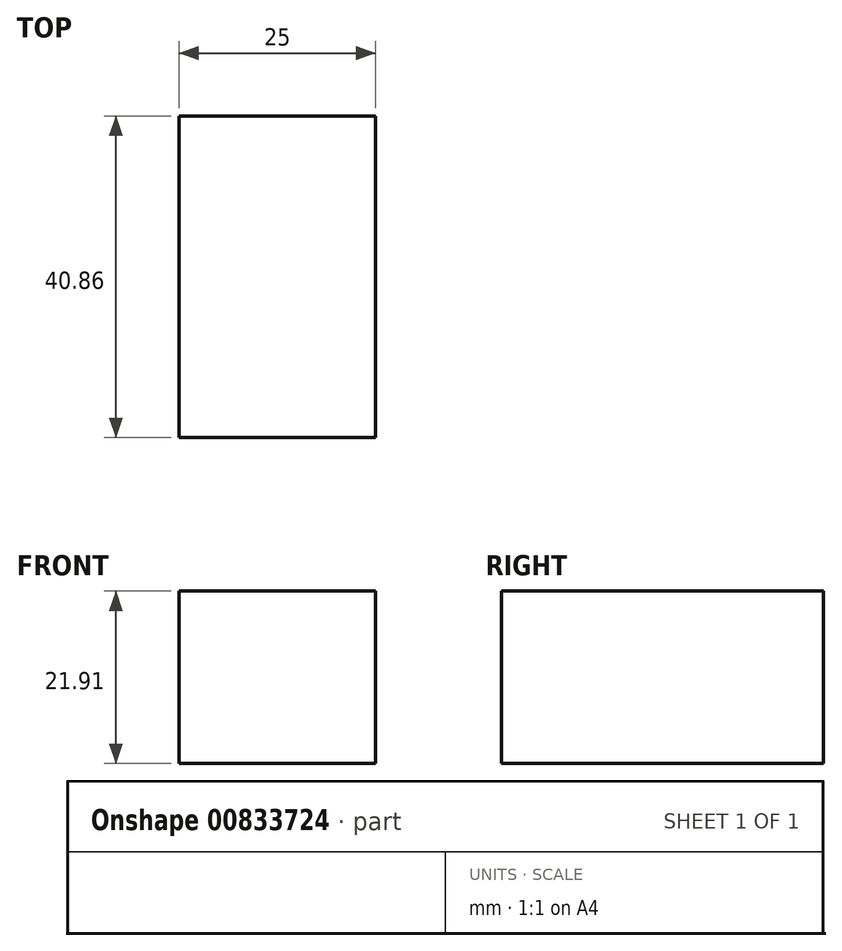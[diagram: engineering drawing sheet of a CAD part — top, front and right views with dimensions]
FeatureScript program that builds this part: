
annotation { "Feature Type Name" : "Feature", "Feature Type Description" : "" }
export const myFeature = defineFeature(function(context is Context, id is Id, definition is map)
    precondition{}
    {
        {
            var Q0;
            Q0=qCreatedBy(makeId("Right.planeOp"),FACE);
            var sketch = newSketch(context, id + "F0", { "sketchPlane" : qUnion([Q0])});
            skLineSegment(sketch, "E0.bottom", {"start": v(-33.9, 41.3) * mm, "end": v(6.96, 41.3) * mm});
            skLineSegment(sketch, "E0.top", {"start": v(-33.9, 19.4) * mm, "end": v(6.96, 19.4) * mm});
            skLineSegment(sketch, "E0.left", {"start": v(-33.9, 41.3) * mm, "end": v(-33.9, 19.4) * mm});
            skLineSegment(sketch, "E0.right", {"start": v(6.96, 41.3) * mm, "end": v(6.96, 19.4) * mm});
            skSolve(sketch);
        }
        {
            var Q0;
            Q0=makeQuery(id+"F0.imprint","IMPRINT",FACE,{"disambiguationData":[TD([[makeQuery(id+"F0.imprint","IMPRINT",EDGE,{"derivedFrom":sQuery(id+"F0.wireOp",EDGE,"E0.bottom")}),-1.0]])]});
            extrude(context, id + "F1", {"entities" : qUnion([Q0]), "depth" : 25 * mm, "offsetDistance" : 25 * mm});
        }
    });
